# Revit family: Electronics_Touch-Panel-Controllers_Biamp_Impera_Tango__
name_source: partatom
category: Communication Devices
units: mm (PartAtom-declared; Revit-internal decimal feet)

## family parameters
Cut with Voids When Loaded = No
Host = Face
Maintain Annotation Orientation = No
OmniClass Number = 23.85.10.17.11
OmniClass Title = Audio-Visual System Components
Part Type = Normal
Room Calculation Point = No
Round Connector Dimension = Use Diameter
Shared = No

## types (1)
- Tango
    Altitude = 0-6,600 ft (0-2000m) MSL
    Apparent Load = 0 VA
    Baud Rate = 1200 – 115200 bit/sec
    Compliance = FCC Part 15B (USA), UL listed (USA and Canada), CE Marked (Europe), RoHS Directive (Europe)
    Connector Description = PoE (IEEE 802.3at Class 3, 15W)
    Connector GPIO = 5-pin, 0.3-inch Euroblock
    Connector RS-232 / IR = 3-pin, 0.3-inch Euroblock
    Connector Relays = 2-pin, 0.3-inch Euroblock
    Cooling = Convection
    Data Bits = 7, 8
    Default Elevation = 48 "
    Depth = 2.8 "
    Description = Impera™ Tango Controller
    Height = 1.4 "
    Housing Material = Biamp - Metal - Black
    Humidity = 10-90% relative humidity (non-condensing)
    IR Frequency Range = 400 Hz to 500 kHz
    Impera Tango = Yes
    Input Trigger High = > 4VDC
    Input Trigger Low = < 1VDC
    Isolation = No
    Manufacturer = Biamp
    Max Current = 0.5A
    Max Power Consumption = 0 W
    Max Voltage = 24VDC
    Model = Impera Tango
    Network Connection = RJ-45 with Ethernet (CAT5e or better)
    Number of Poles = 1
    Number of Ports GPIO = 8
    Number of Ports RS-232 / IR = 3 (bi-directional); 2 (uni-directional)
    Parity = Even, Odd, None
    Power Factor = 1
    Product Documentation Link = https://downloads.biamp.com
    Product Page URL = https://www.biamp.com
    Product data url = https://www.bimobject.com
    Relays Quantity = 4
    Relays power capacity = 30VDC / 0.5A
    Stop Bits = 1, 2
    Temperature Range = 32 - 86° F (0 – 30° C)
    Type = Open drain
    URL = https://www.biamp.com
    Voltage = 0 V
    Weight = 1.10 lbf
    Width = 8.7 "

## geometry (parser evidence)
native form markers: Sweep x2
no freeform markers — native parametric forms only
